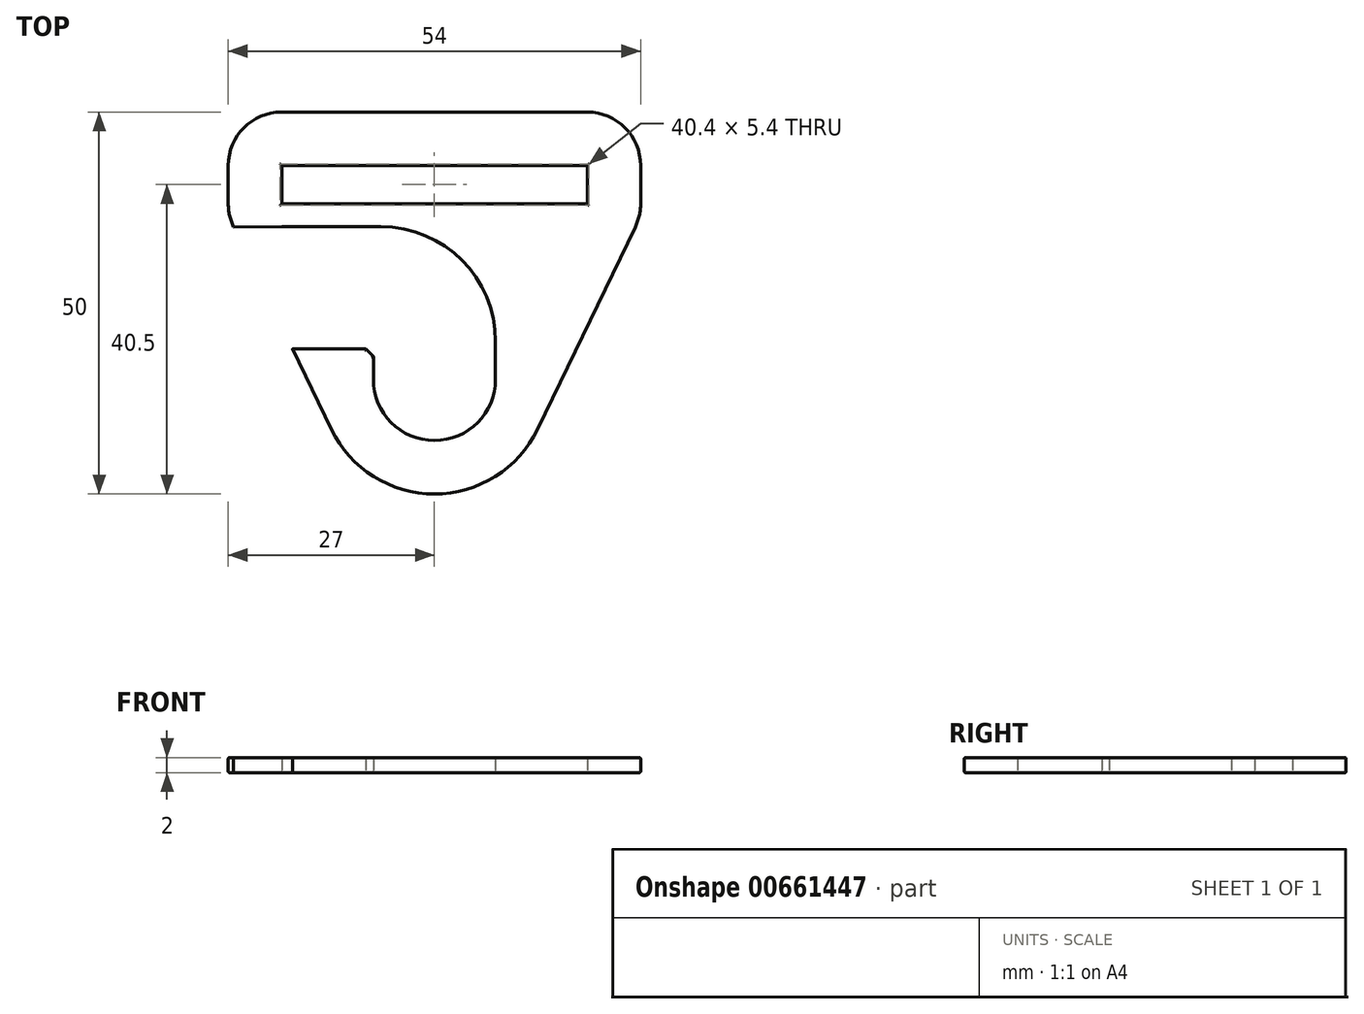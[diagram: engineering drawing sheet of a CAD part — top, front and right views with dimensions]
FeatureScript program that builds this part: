
annotation { "Feature Type Name" : "Feature", "Feature Type Description" : "" }
export const myFeature = defineFeature(function(context is Context, id is Id, definition is map)
    precondition{}
    {
        {
            var Q0;
            Q0=qCreatedBy(makeId("Top.planeOp"),FACE);
            var sketch = newSketch(context, id + "F0", { "sketchPlane" : qUnion([Q0])});
            skLineSegment(sketch, "E0.bottom", {"start": v(0, 12) * mm, "end": v(-20, 12) * mm});
            skLineSegment(sketch, "E0.top", {"start": v(0, 5) * mm, "end": v(-20, 5) * mm});
            skLineSegment(sketch, "E0.left", {"start": v(0, 12) * mm, "end": v(0, 5) * mm});
            skLineSegment(sketch, "E0.right", {"start": v(-20, 12) * mm, "end": v(-20, 5) * mm});
            skLineSegment(sketch, "E1.bottom", {"start": v(0, 12) * mm, "end": v(20, 12) * mm});
            skLineSegment(sketch, "E1.top", {"start": v(0, 5) * mm, "end": v(20, 5) * mm});
            skLineSegment(sketch, "E1.right", {"start": v(20, 12) * mm, "end": v(20, 5) * mm});
            skLineSegment(sketch, "E2.bottom", {"start": v(20, 12) * mm, "end": v(27, 12) * mm});
            skLineSegment(sketch, "E2.top", {"start": v(20, 5) * mm, "end": v(27, 5) * mm});
            skLineSegment(sketch, "E2.right", {"start": v(27, 12) * mm, "end": v(27, 5) * mm});
            skLineSegment(sketch, "E3.bottom", {"start": v(-20, 12) * mm, "end": v(-27, 12) * mm});
            skLineSegment(sketch, "E3.top", {"start": v(-20, 5) * mm, "end": v(-27, 5) * mm});
            skLineSegment(sketch, "E3.right", {"start": v(-27, 12) * mm, "end": v(-27, 5) * mm});
            skLineSegment(sketch, "E4.top", {"start": v(20, 0) * mm, "end": v(27, 0) * mm});
            skLineSegment(sketch, "E4.left", {"start": v(20, 5) * mm, "end": v(20, 0) * mm});
            skLineSegment(sketch, "E4.right", {"start": v(27, 5) * mm, "end": v(27, 0) * mm});
            skLineSegment(sketch, "E5.top", {"start": v(-20, 0) * mm, "end": v(-27, 0) * mm});
            skLineSegment(sketch, "E5.left", {"start": v(-20, 5) * mm, "end": v(-20, 0) * mm});
            skLineSegment(sketch, "E5.right", {"start": v(-27, 5) * mm, "end": v(-27, 0) * mm});
            skLineSegment(sketch, "E6.bottom", {"start": v(-20, 0) * mm, "end": v(20, 0) * mm});
            skLineSegment(sketch, "E6.top", {"start": v(-20, -3) * mm, "end": v(-7, -3) * mm});
            skLineSegment(sketch, "E7", {"start": v(0, 5) * mm, "end": v(0, 0) * mm});
            skArc(sketch, "E8", {"start": v(-8, -23) * mm, "mid": v(0, -31) * mm, "end": v(8, -23) * mm});
            skLineSegment(sketch, "E9", {"start": v(27, 0) * mm, "end": v(27, -1.6) * mm});
            skLineSegment(sketch, "E10", {"start": v(-27, 0) * mm, "end": v(-27, -1.6) * mm});
            skLineSegment(sketch, "E11", {"start": v(13.5, -29.53) * mm, "end": v(27, -1.6) * mm});
            skPoint(sketch, "E12", {"position": v(27, -1.6) * mm});
            skLineSegment(sketch, "E13", {"start": v(-13.5, -29.53) * mm, "end": v(-18.6, -19) * mm});
            skPoint(sketch, "E14", {"position": v(-27, -1.6) * mm});
            skArc(sketch, "E15", {"start": v(13.5, -29.53) * mm, "mid": v(0, -38) * mm, "end": v(-13.5, -29.53) * mm});
            skLineSegment(sketch, "E16", {"start": v(8, -23) * mm, "end": v(8, -18) * mm});
            skArc(sketch, "E17", {"start": v(8, -18) * mm, "mid": v(3.6, -7.4) * mm, "end": v(-7, -3) * mm});
            skLineSegment(sketch, "E18", {"start": v(-8, -23) * mm, "end": v(-8, -20) * mm});
            skLineSegment(sketch, "E19", {"start": v(-9, -19) * mm, "end": v(-8, -20) * mm});
            skLineSegment(sketch, "E20", {"start": v(-9, -19) * mm, "end": v(-18.6, -19) * mm});
            skPoint(sketch, "E21", {"position": v(-10.82, -19) * mm});
            skPoint(sketch, "E22.end.orphan", {"position": v(7.2, -26.48) * mm});
            skPoint(sketch, "E23", {"position": v(-18.55, -3) * mm});
            skLineSegment(sketch, "E24", {"start": v(-26.3, -3.05) * mm, "end": v(-20, -3) * mm});
            skLineSegment(sketch, "E25.trimOffspring", {"start": v(-26.3, -3.05) * mm, "end": v(-27, -1.6) * mm});
            skSolve(sketch);
        }
        {
            var Q0;
            Q0=makeQuery(id+"F0.imprint","IMPRINT",FACE,{"disambiguationData":[TD([[makeQuery(id+"F0.imprint","IMPRINT",EDGE,{"derivedFrom":sQuery(id+"F0.wireOp",EDGE,"E3.bottom")}),1.0]])]});
            var Q1;
            Q1=makeQuery(id+"F0.imprint","IMPRINT",FACE,{"disambiguationData":[TD([[makeQuery(id+"F0.imprint","IMPRINT",EDGE,{"derivedFrom":sQuery(id+"F0.wireOp",EDGE,"E0.bottom")}),1.0]])]});
            var Q2;
            Q2=makeQuery(id+"F0.imprint","IMPRINT",FACE,{"disambiguationData":[TD([[makeQuery(id+"F0.imprint","IMPRINT",EDGE,{"derivedFrom":sQuery(id+"F0.wireOp",EDGE,"E1.bottom")}),-1.0]])]});
            var Q3;
            Q3=makeQuery(id+"F0.imprint","IMPRINT",FACE,{"disambiguationData":[TD([[makeQuery(id+"F0.imprint","IMPRINT",EDGE,{"derivedFrom":sQuery(id+"F0.wireOp",EDGE,"E2.bottom")}),-1.0]])]});
            var Q4;
            Q4=makeQuery(id+"F0.imprint","IMPRINT",FACE,{"disambiguationData":[TD([[makeQuery(id+"F0.imprint","IMPRINT",EDGE,{"derivedFrom":sQuery(id+"F0.wireOp",EDGE,"E2.top")}),-1.0]])]});
            var Q5;
            {var subQ0=sQuery(id+"F0.wireOp",EDGE,"E4.top");Q5=makeQuery(id+"F0.imprint","IMPRINT",FACE,{"disambiguationData":[TD([[makeQuery(id+"F0.imprint","IMPRINT",EDGE,{"derivedFrom":subQ0}),-1.0]])]});}
            var Q6;
            Q6=makeQuery(id+"F0.imprint","IMPRINT",FACE,{"disambiguationData":[TD([[makeQuery(id+"F0.imprint","IMPRINT",EDGE,{"derivedFrom":sQuery(id+"F0.wireOp",EDGE,"E3.top")}),1.0]])]});
            extrude(context, id + "F1", {"entities" : qUnion([Q0, Q1, Q2, Q3, Q4, Q5, Q6]), "depth" : 2 * mm, "offsetDistance" : 25 * mm});
        }
        {
            var Q0;
            Q0=makeQuery(id+"F1.opExtrude","SWEPT_EDGE",EDGE,{"disambiguationData":[OSD([sQuery(id+"F0.wireOp",EDGE,"E3.bottom"),sQuery(id+"F0.wireOp",EDGE,"E3.right")])]});
            var Q1;
            Q1=makeQuery(id+"F1.opExtrude","SWEPT_EDGE",EDGE,{"disambiguationData":[OSD([sQuery(id+"F0.wireOp",EDGE,"E2.bottom"),sQuery(id+"F0.wireOp",EDGE,"E2.right")])]});
            var Q2;
            Q2=makeQuery(id+"F1.opExtrude","SWEPT_EDGE",EDGE,{"disambiguationData":[OSD([sQuery(id+"F0.wireOp",EDGE,"E9"),sQuery(id+"F0.wireOp",EDGE,"E11")])]});
            var Q3;
            Q3=makeQuery(id+"F1.opExtrude","SWEPT_EDGE",EDGE,{"disambiguationData":[OSD([sQuery(id+"F0.wireOp",EDGE,"E10"),sQuery(id+"F0.wireOp",EDGE,"E25.trimOffspring")])]});
            fillet(context, id + "F2", {"entities" : qUnion([Q0, Q1, Q2, Q3]), "radius" : 7 * mm, "tangentPropagation" : true, "allowEdgeOverflow" : false});
        }
        {
            var Q0;
            Q0=makeQuery(id+"F1.opExtrude","CAP_FACE",FACE,{"disambiguationData":[OSD([sQuery(id+"F0.wireOp",EDGE,"E0.bottom"),sQuery(id+"F0.wireOp",EDGE,"E0.top"),sQuery(id+"F0.wireOp",EDGE,"E1.bottom"),sQuery(id+"F0.wireOp",EDGE,"E1.top"),sQuery(id+"F0.wireOp",EDGE,"E2.bottom"),sQuery(id+"F0.wireOp",EDGE,"E2.right"),sQuery(id+"F0.wireOp",EDGE,"E3.bottom"),sQuery(id+"F0.wireOp",EDGE,"E3.right"),sQuery(id+"F0.wireOp",EDGE,"E4.left"),sQuery(id+"F0.wireOp",EDGE,"E4.right"),sQuery(id+"F0.wireOp",EDGE,"E5.left"),sQuery(id+"F0.wireOp",EDGE,"E5.right"),sQuery(id+"F0.wireOp",EDGE,"E6.bottom"),sQuery(id+"F0.wireOp",EDGE,"E6.top"),sQuery(id+"F0.wireOp",EDGE,"E8"),sQuery(id+"F0.wireOp",EDGE,"E9"),sQuery(id+"F0.wireOp",EDGE,"E10"),sQuery(id+"F0.wireOp",EDGE,"E11"),sQuery(id+"F0.wireOp",EDGE,"E13"),sQuery(id+"F0.wireOp",EDGE,"E15"),sQuery(id+"F0.wireOp",EDGE,"E16"),sQuery(id+"F0.wireOp",EDGE,"E17"),sQuery(id+"F0.wireOp",EDGE,"E18"),sQuery(id+"F0.wireOp",EDGE,"E19"),sQuery(id+"F0.wireOp",EDGE,"E20"),sQuery(id+"F0.wireOp",EDGE,"E24"),sQuery(id+"F0.wireOp",EDGE,"E25.trimOffspring")])],"isStart":false});
            var Q1;
            Q1=makeQuery(id+"F1.opExtrude","CAP_FACE",FACE,{"disambiguationData":[OSD([sQuery(id+"F0.wireOp",EDGE,"E0.bottom"),sQuery(id+"F0.wireOp",EDGE,"E0.top"),sQuery(id+"F0.wireOp",EDGE,"E1.bottom"),sQuery(id+"F0.wireOp",EDGE,"E1.top"),sQuery(id+"F0.wireOp",EDGE,"E2.bottom"),sQuery(id+"F0.wireOp",EDGE,"E2.right"),sQuery(id+"F0.wireOp",EDGE,"E3.bottom"),sQuery(id+"F0.wireOp",EDGE,"E3.right"),sQuery(id+"F0.wireOp",EDGE,"E4.left"),sQuery(id+"F0.wireOp",EDGE,"E4.right"),sQuery(id+"F0.wireOp",EDGE,"E5.left"),sQuery(id+"F0.wireOp",EDGE,"E5.right"),sQuery(id+"F0.wireOp",EDGE,"E6.bottom"),sQuery(id+"F0.wireOp",EDGE,"E6.top"),sQuery(id+"F0.wireOp",EDGE,"E8"),sQuery(id+"F0.wireOp",EDGE,"E9"),sQuery(id+"F0.wireOp",EDGE,"E10"),sQuery(id+"F0.wireOp",EDGE,"E11"),sQuery(id+"F0.wireOp",EDGE,"E13"),sQuery(id+"F0.wireOp",EDGE,"E15"),sQuery(id+"F0.wireOp",EDGE,"E16"),sQuery(id+"F0.wireOp",EDGE,"E17"),sQuery(id+"F0.wireOp",EDGE,"E18"),sQuery(id+"F0.wireOp",EDGE,"E19"),sQuery(id+"F0.wireOp",EDGE,"E20"),sQuery(id+"F0.wireOp",EDGE,"E24"),sQuery(id+"F0.wireOp",EDGE,"E25.trimOffspring")])],"isStart":true});
            fillet(context, id + "F3", {"entities" : qUnion([Q0, Q1]), "tangentPropagation" : true, "radius" : 0.2 * mm, "defaultsChanged" : false, "vertexSettings" : [], "allowEdgeOverflow" : false});
        }
    });
